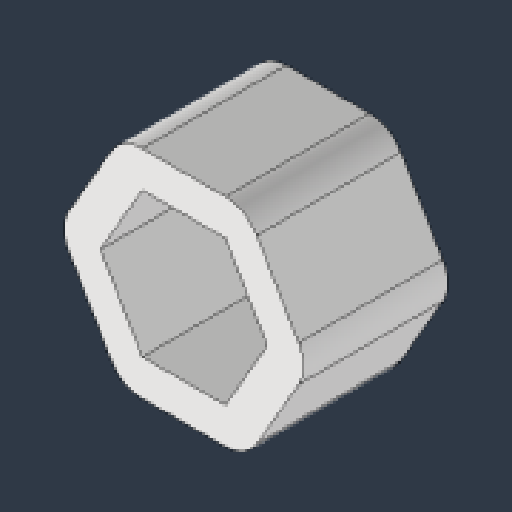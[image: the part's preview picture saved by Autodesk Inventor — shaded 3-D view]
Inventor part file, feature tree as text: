
AUTODESK INVENTOR PART (.ipt)
format: ipt  version: 2024.3 (Build 283343000, 343)  size: 115,200 bytes
history: native  units: in
note: dims shown in document units (in); Inventor stores cm internally (conversion verified against a paired STEP export)
features: extrude x1, fillet x1, sketch x1
ambient origin geometry x8: Origin, YZ Plane, XZ Plane, XY Plane, X Axis, Y Axis, Z Axis, Center Point
bodies: Solid1 (feature_tree)
feature tree (3):
  extrude  "Extrusion1"  Depth=0.125in
  fillet  "Fillet1"  Radius=0.5in
  sketch  "Sketch1"  dims[d0=0.501in d1=0.125in d2=0.5in d3=0.0in d4=0.125in]
